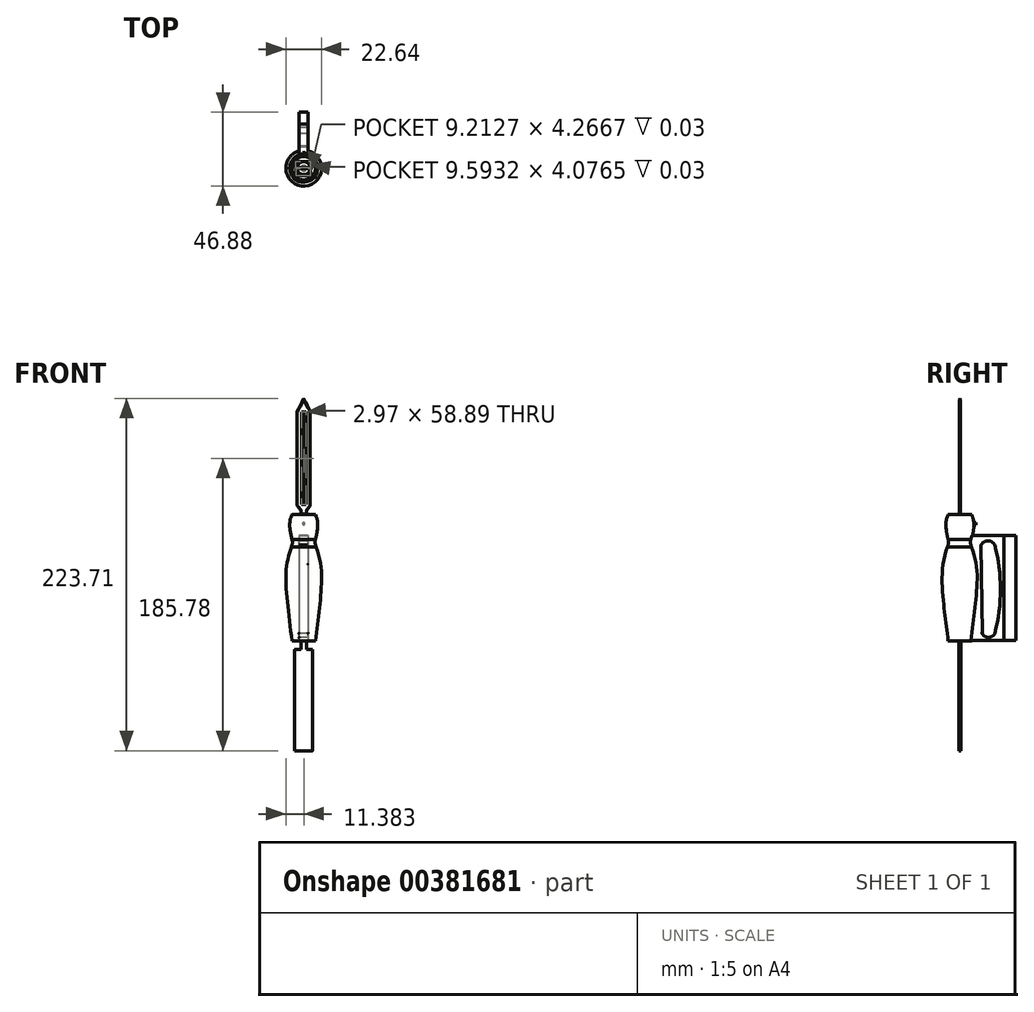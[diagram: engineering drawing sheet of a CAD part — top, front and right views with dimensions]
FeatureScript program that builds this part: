
annotation { "Feature Type Name" : "Feature", "Feature Type Description" : "" }
export const myFeature = defineFeature(function(context is Context, id is Id, definition is map)
    precondition{}
    {
        {
            var Q0;
            Q0=qCreatedBy(makeId("Front.planeOp"),FACE);
            var sketch = newSketch(context, id + "F0", { "sketchPlane" : qUnion([Q0])});
            skLineSegment(sketch, "E0", {"start": v(0, 19.44) * mm, "end": v(-7.47, 19.44) * mm});
            skLineSegment(sketch, "E1", {"start": v(-7.47, -61) * mm, "end": v(0, -61) * mm});
            skLineSegment(sketch, "E2", {"start": v(0, -61) * mm, "end": v(0, 19.44) * mm});
            skPoint(sketch, "E3.2.internal.orphan", {"position": v(-7.47, 3.27) * mm});
            skPoint(sketch, "E3.6.internal.orphan", {"position": v(-7.47, -61) * mm});
            skPoint(sketch, "E4.3.internal.orphan", {"position": v(-7.47, 0) * mm});
            skFitSpline(sketch, "E5", {"points": [v(-7.47, 19.44) * mm, v(-10.1, 11.25) * mm, v(-7.47, 3.27) * mm, v(-7.47, 0) * mm, v(-10.82, -8.71) * mm, v(-14.15, -22.97) * mm, v(-7.47, -61) * mm], "startDerivative": vector(-30.18, -56.03) * mm, "endDerivative": vector(34.52, -142.2) * mm});
            skFitSpline(sketch, "E6", {"points": [v(-7.47, 0) * mm, v(-10.82, -13.11) * mm, v(-10.82, -31.68) * mm, v(-7.47, -61) * mm], "startDerivative": vector(-14.77, -46.17) * mm, "endDerivative": vector(9.76, -75.95) * mm});
            skFitSpline(sketch, "E7", {"points": [v(-7.47, 19.44) * mm, v(-8.89, 13.54) * mm, v(-7.47, 3.27) * mm], "startDerivative": vector(-4.54, -12.63) * mm, "endDerivative": vector(4.15, -19.4) * mm});
            skSolve(sketch);
        }
        {
            var Q0;
            Q0=makeQuery(id+"F0.imprint","IMPRINT",FACE,{"disambiguationData":[TD([[makeQuery(id+"F0.imprint","IMPRINT",EDGE,{"derivedFrom":sQuery(id+"F0.wireOp",EDGE,"E0")}),1.0]])]});
            var Q1;
            Q1=sQuery(id+"F0.wireOp",EDGE,"E2");
            revolve(context, id + "F1", {"entities" : qUnion([Q0]), "axis" : qUnion([Q1]), "revolveType" : RevolveType.FULL});
        }
        {
            var Q0;
            Q0=qCreatedBy(makeId("Front.planeOp"),FACE);
            var sketch = newSketch(context, id + "F2", { "sketchPlane" : qUnion([Q0])});
            skLineSegment(sketch, "E8", {"start": v(0, 19.46) * mm, "end": v(0, 92.9) * mm});
            skLineSegment(sketch, "E9", {"start": v(0, 92.9) * mm, "end": v(-4.15, 84.7) * mm});
            skLineSegment(sketch, "E10", {"start": v(-4.15, 84.7) * mm, "end": v(-4.15, 24.88) * mm});
            skLineSegment(sketch, "E11", {"start": v(-4.15, 24.88) * mm, "end": v(-1.84, 21.73) * mm});
            skLineSegment(sketch, "E12", {"start": v(-1.84, 21.73) * mm, "end": v(-1.84, 19.45) * mm});
            skLineSegment(sketch, "E13", {"start": v(-1.84, 19.45) * mm, "end": v(0, 19.46) * mm});
            skSolve(sketch);
        }
        {
            var Q0;
            Q0=makeQuery(id+"F2.imprint","IMPRINT",FACE,{"disambiguationData":[TD([[makeQuery(id+"F2.imprint","IMPRINT",EDGE,{"derivedFrom":sQuery(id+"F2.wireOp",EDGE,"E8")}),1.0]])]});
            var Q1;
            Q1=sQuery(id+"F2.wireOp",EDGE,"E8");
            revolve(context, id + "F3", {"entities" : qUnion([Q0]), "axis" : qUnion([Q1]), "revolveType" : RevolveType.FULL});
        }
        {
            var Q0;
            Q0=qCreatedBy(makeId("Top.planeOp"),FACE);
            cPlane(context, id + "F4", {"entities" : qUnion([Q0]), "cplaneType" : CPlaneType.OFFSET, "offset" : 93.73 * mm, "width" : 152.4 * mm, "height" : 152.4 * mm});
        }
        {
            var Q0;
            Q0=qCreatedBy(id+"F4.planeOp",FACE);
            var sketch = newSketch(context, id + "F5", { "sketchPlane" : qUnion([Q0])});
            skLineSegment(sketch, "E14.bottom", {"start": v(4.35, -0.27) * mm, "end": v(-4.87, -0.27) * mm});
            skLineSegment(sketch, "E14.top", {"start": v(4.35, -4.54) * mm, "end": v(-4.87, -4.54) * mm});
            skLineSegment(sketch, "E14.left", {"start": v(4.35, -0.27) * mm, "end": v(4.35, -4.54) * mm});
            skLineSegment(sketch, "E14.right", {"start": v(-4.87, -0.27) * mm, "end": v(-4.87, -4.54) * mm});
            skLineSegment(sketch, "E15.bottom", {"start": v(4.37, 0.27) * mm, "end": v(-5.22, 0.27) * mm});
            skLineSegment(sketch, "E15.top", {"start": v(4.37, 4.35) * mm, "end": v(-5.22, 4.35) * mm});
            skLineSegment(sketch, "E15.left", {"start": v(4.37, 0.27) * mm, "end": v(4.37, 4.35) * mm});
            skLineSegment(sketch, "E15.right", {"start": v(-5.22, 0.27) * mm, "end": v(-5.22, 4.35) * mm});
            skSolve(sketch);
        }
        {
            var Q0;
            Q0=makeQuery(id+"F5.imprint","IMPRINT",FACE,{"disambiguationData":[TD([[makeQuery(id+"F5.imprint","IMPRINT",EDGE,{"derivedFrom":sQuery(id+"F5.wireOp",EDGE,"E15.bottom")}),-1.0]])]});
            var Q1;
            Q1=makeQuery(id+"F5.imprint","IMPRINT",FACE,{"disambiguationData":[TD([[makeQuery(id+"F5.imprint","IMPRINT",EDGE,{"derivedFrom":sQuery(id+"F5.wireOp",EDGE,"E14.bottom")}),1.0]])]});
            extrude(context, id + "F6", {"entities" : qUnion([Q0, Q1]), "operationType" : NewBodyOperationType.REMOVE, "oppositeDirection" : true, "depth" : 74.32 * mm});
        }
        {
            var Q0;
            Q0=qCreatedBy(makeId("Front.planeOp"),FACE);
            cPlane(context, id + "F7", {"entities" : qUnion([Q0]), "cplaneType" : CPlaneType.OFFSET, "offset" : 18.29 * mm, "width" : 152.4 * mm, "height" : 152.4 * mm});
        }
        {
            var Q0;
            Q0=qCreatedBy(id+"F7.planeOp",FACE);
            var sketch = newSketch(context, id + "F8", { "sketchPlane" : qUnion([Q0])});
            skLineSegment(sketch, "E16.bottom", {"start": v(-1.17, 84.42) * mm, "end": v(1.3, 84.42) * mm});
            skLineSegment(sketch, "E16.top", {"start": v(-1.17, 25.54) * mm, "end": v(1.3, 25.54) * mm});
            skLineSegment(sketch, "E16.left", {"start": v(-1.17, 84.42) * mm, "end": v(-1.17, 25.54) * mm});
            skLineSegment(sketch, "E16.right", {"start": v(1.3, 84.42) * mm, "end": v(1.3, 25.54) * mm});
            skSolve(sketch);
        }
        {
            var Q0;
            Q0=makeQuery(id+"F8.imprint","IMPRINT",FACE,{"disambiguationData":[TD([[makeQuery(id+"F8.imprint","IMPRINT",EDGE,{"derivedFrom":sQuery(id+"F8.wireOp",EDGE,"E16.bottom")}),-1.0]])]});
            extrude(context, id + "F9", {"entities" : qUnion([Q0]), "operationType" : NewBodyOperationType.REMOVE, "oppositeDirection" : true, "depth" : 25.4 * mm});
        }
        {
            var Q0;
            Q0=makeQuery(id+"F6.boolean.opBoolean","INTERSECT",EDGE,{"derivedFrom":[makeQuery(id+"F3.opRevolve","SWEPT_FACE",FACE,{"disambiguationData":[OSD([sQuery(id+"F2.wireOp",EDGE,"E9")])]}),makeQuery(id+"F6.opExtrude","SWEPT_FACE",FACE,{"disambiguationData":[OSD([sQuery(id+"F5.wireOp",EDGE,"E14.bottom")])]})]});
            var Q1;
            Q1=makeQuery(id+"F6.boolean.opBoolean","INTERSECT",EDGE,{"disambiguationData":[OD(1.0)],"derivedFrom":[makeQuery(id+"F3.opRevolve","SWEPT_FACE",FACE,{"disambiguationData":[OSD([sQuery(id+"F2.wireOp",EDGE,"E10")])]}),makeQuery(id+"F6.opExtrude","SWEPT_FACE",FACE,{"disambiguationData":[OSD([sQuery(id+"F5.wireOp",EDGE,"E14.bottom")])]})]});
            var Q2;
            Q2=makeQuery(id+"F6.boolean.opBoolean","INTERSECT",EDGE,{"disambiguationData":[OD(0.0)],"derivedFrom":[makeQuery(id+"F3.opRevolve","SWEPT_FACE",FACE,{"disambiguationData":[OSD([sQuery(id+"F2.wireOp",EDGE,"E10")])]}),makeQuery(id+"F6.opExtrude","SWEPT_FACE",FACE,{"disambiguationData":[OSD([sQuery(id+"F5.wireOp",EDGE,"E14.bottom")])]})]});
            var Q3;
            Q3=makeQuery(id+"F6.boolean.opBoolean","INTERSECT",EDGE,{"disambiguationData":[OD(0.0)],"derivedFrom":[makeQuery(id+"F3.opRevolve","SWEPT_FACE",FACE,{"disambiguationData":[OSD([sQuery(id+"F2.wireOp",EDGE,"E11")])]}),makeQuery(id+"F6.opExtrude","SWEPT_FACE",FACE,{"disambiguationData":[OSD([sQuery(id+"F5.wireOp",EDGE,"E14.bottom")])]})]});
            var Q4;
            Q4=makeQuery(id+"F6.boolean.opBoolean","INTERSECT",EDGE,{"disambiguationData":[OD(1.0)],"derivedFrom":[makeQuery(id+"F3.opRevolve","SWEPT_FACE",FACE,{"disambiguationData":[OSD([sQuery(id+"F2.wireOp",EDGE,"E11")])]}),makeQuery(id+"F6.opExtrude","SWEPT_FACE",FACE,{"disambiguationData":[OSD([sQuery(id+"F5.wireOp",EDGE,"E14.bottom")])]})]});
            var Q5;
            Q5=makeQuery(id+"F6.boolean.opBoolean","INTERSECT",EDGE,{"derivedFrom":[makeQuery(id+"F3.opRevolve","SWEPT_FACE",FACE,{"disambiguationData":[OSD([sQuery(id+"F2.wireOp",EDGE,"E9")])]}),makeQuery(id+"F6.opExtrude","SWEPT_FACE",FACE,{"disambiguationData":[OSD([sQuery(id+"F5.wireOp",EDGE,"E15.bottom")])]})]});
            var Q6;
            Q6=makeQuery(id+"F6.boolean.opBoolean","INTERSECT",EDGE,{"disambiguationData":[OD(0.0)],"derivedFrom":[makeQuery(id+"F3.opRevolve","SWEPT_FACE",FACE,{"disambiguationData":[OSD([sQuery(id+"F2.wireOp",EDGE,"E10")])]}),makeQuery(id+"F6.opExtrude","SWEPT_FACE",FACE,{"disambiguationData":[OSD([sQuery(id+"F5.wireOp",EDGE,"E15.bottom")])]})]});
            var Q7;
            Q7=makeQuery(id+"F6.boolean.opBoolean","SPLIT",FACE,{"disambiguationData":[OD(1.0)],"derivedFrom":makeQuery(id+"F3.opRevolve","SWEPT_FACE",FACE,{"disambiguationData":[OSD([sQuery(id+"F2.wireOp",EDGE,"E10")])]})});
            var Q8;
            Q8=makeQuery(id+"F6.boolean.opBoolean","INTERSECT",EDGE,{"disambiguationData":[OD(1.0)],"derivedFrom":[makeQuery(id+"F3.opRevolve","SWEPT_FACE",FACE,{"disambiguationData":[OSD([sQuery(id+"F2.wireOp",EDGE,"E11")])]}),makeQuery(id+"F6.opExtrude","SWEPT_FACE",FACE,{"disambiguationData":[OSD([sQuery(id+"F5.wireOp",EDGE,"E15.bottom")])]})]});
            var Q9;
            Q9=makeQuery(id+"F6.boolean.opBoolean","INTERSECT",EDGE,{"disambiguationData":[OD(0.0)],"derivedFrom":[makeQuery(id+"F3.opRevolve","SWEPT_FACE",FACE,{"disambiguationData":[OSD([sQuery(id+"F2.wireOp",EDGE,"E11")])]}),makeQuery(id+"F6.opExtrude","SWEPT_FACE",FACE,{"disambiguationData":[OSD([sQuery(id+"F5.wireOp",EDGE,"E15.bottom")])]})]});
            fillet(context, id + "F10", {"entities" : qUnion([Q0, Q1, Q2, Q3, Q4, Q5, Q6, Q7, Q8, Q9]), "radius" : 0.25 * mm, "tangentPropagation" : true, "allowEdgeOverflow" : false});
        }
        {
            var Q0;
            Q0=makeQuery(id+"F9.boolean.opBoolean","INTERSECT",EDGE,{"derivedFrom":[makeQuery(id+"F6.boolean.opBoolean","COPY",FACE,{"derivedFrom":makeQuery(id+"F6.opExtrude","SWEPT_FACE",FACE,{"disambiguationData":[OSD([sQuery(id+"F5.wireOp",EDGE,"E15.bottom")])]})}),makeQuery(id+"F9.opExtrude","SWEPT_FACE",FACE,{"disambiguationData":[OSD([sQuery(id+"F8.wireOp",EDGE,"E16.right")])]})]});
            var Q1;
            Q1=makeQuery(id+"F9.boolean.opBoolean","INTERSECT",EDGE,{"derivedFrom":[makeQuery(id+"F6.boolean.opBoolean","COPY",FACE,{"derivedFrom":makeQuery(id+"F6.opExtrude","SWEPT_FACE",FACE,{"disambiguationData":[OSD([sQuery(id+"F5.wireOp",EDGE,"E15.bottom")])]})}),makeQuery(id+"F9.opExtrude","SWEPT_FACE",FACE,{"disambiguationData":[OSD([sQuery(id+"F8.wireOp",EDGE,"E16.left")])]})]});
            var Q2;
            Q2=makeQuery(id+"F9.boolean.opBoolean","INTERSECT",EDGE,{"derivedFrom":[makeQuery(id+"F6.boolean.opBoolean","COPY",FACE,{"derivedFrom":makeQuery(id+"F6.opExtrude","SWEPT_FACE",FACE,{"disambiguationData":[OSD([sQuery(id+"F5.wireOp",EDGE,"E14.bottom")])]})}),makeQuery(id+"F9.opExtrude","SWEPT_FACE",FACE,{"disambiguationData":[OSD([sQuery(id+"F8.wireOp",EDGE,"E16.left")])]})]});
            var Q3;
            Q3=makeQuery(id+"F9.boolean.opBoolean","INTERSECT",EDGE,{"derivedFrom":[makeQuery(id+"F6.boolean.opBoolean","COPY",FACE,{"derivedFrom":makeQuery(id+"F6.opExtrude","SWEPT_FACE",FACE,{"disambiguationData":[OSD([sQuery(id+"F5.wireOp",EDGE,"E14.bottom")])]})}),makeQuery(id+"F9.opExtrude","SWEPT_FACE",FACE,{"disambiguationData":[OSD([sQuery(id+"F8.wireOp",EDGE,"E16.right")])]})]});
            chamfer(context, id + "F11", {"entities" : qUnion([Q0, Q1, Q2, Q3]), "width" : 0.25 * mm, "tangentPropagation" : true});
        }
        {
            var Q0;
            Q0=qCreatedBy(makeId("Front.planeOp"),FACE);
            cPlane(context, id + "F12", {"entities" : qUnion([Q0]), "cplaneType" : CPlaneType.OFFSET, "offset" : 8.79 * mm, "oppositeDirection" : true, "width" : 152.4 * mm, "height" : 152.4 * mm});
        }
        {
            var Q0;
            Q0=qCreatedBy(id+"F12.planeOp",FACE);
            var sketch = newSketch(context, id + "F13", { "sketchPlane" : qUnion([Q0])});
            skCircle(sketch, "E17", {"center": v(0, 13.43) * mm, "radius": 0.68 * mm});
            skSolve(sketch);
        }
        {
            var Q0;
            Q0=makeQuery(id+"F13.imprint","IMPRINT",FACE,{"disambiguationData":[TD([[makeQuery(id+"F13.imprint","IMPRINT",EDGE,{"derivedFrom":sQuery(id+"F13.wireOp",EDGE,"E17")}),1.0]])]});
            extrude(context, id + "F14", {"entities" : qUnion([Q0]), "operationType" : NewBodyOperationType.ADD, "oppositeDirection" : true, "depth" : 1.24 * mm});
        }
        {
            var Q0;
            Q0=qCreatedBy(makeId("Front.planeOp"),FACE);
            cPlane(context, id + "F15", {"entities" : qUnion([Q0]), "cplaneType" : CPlaneType.OFFSET, "offset" : 6.6 * mm, "oppositeDirection" : true, "width" : 152.4 * mm, "height" : 152.4 * mm});
        }
        {
            var Q0;
            Q0=qCreatedBy(id+"F15.planeOp",FACE);
            var sketch = newSketch(context, id + "F16", { "sketchPlane" : qUnion([Q0])});
            skLineSegment(sketch, "E18.bottom", {"start": v(-3.1, 5.9) * mm, "end": v(2.7, 5.9) * mm});
            skLineSegment(sketch, "E18.top", {"start": v(-3.1, -60.67) * mm, "end": v(2.7, -60.67) * mm});
            skLineSegment(sketch, "E18.left", {"start": v(-3.1, 5.9) * mm, "end": v(-3.1, -60.67) * mm});
            skLineSegment(sketch, "E18.right", {"start": v(2.7, 5.9) * mm, "end": v(2.7, -60.67) * mm});
            skSolve(sketch);
        }
        {
            var Q0;
            Q0=makeQuery(id+"F16.imprint","IMPRINT",FACE,{"disambiguationData":[TD([[makeQuery(id+"F16.imprint","IMPRINT",EDGE,{"derivedFrom":sQuery(id+"F16.wireOp",EDGE,"E18.bottom")}),-1.0]])]});
            extrude(context, id + "F17", {"entities" : qUnion([Q0]), "operationType" : NewBodyOperationType.ADD, "oppositeDirection" : true, "depth" : 21.34 * mm});
        }
        {
            var Q0;
            Q0=qCreatedBy(makeId("Right.planeOp"),FACE);
            cPlane(context, id + "F18", {"entities" : qUnion([Q0]), "cplaneType" : CPlaneType.OFFSET, "offset" : 7.87 * mm, "oppositeDirection" : true, "width" : 152.4 * mm, "height" : 152.4 * mm});
        }
        {
            var Q0;
            Q0=qCreatedBy(id+"F18.planeOp",FACE);
            var sketch = newSketch(context, id + "F19", { "sketchPlane" : qUnion([Q0])});
            skArc(sketch, "E19", {"start": v(22.14, 0) * mm, "mid": v(17.8, 2.52) * mm, "end": v(13.44, 0) * mm});
            skArc(sketch, "E20", {"start": v(22.14, -56.25) * mm, "mid": v(25.8, -28.12) * mm, "end": v(22.14, 0) * mm});
            skArc(sketch, "E21", {"start": v(14.15, -56.25) * mm, "mid": v(18.15, -58.76) * mm, "end": v(22.14, -56.25) * mm});
            skLineSegment(sketch, "E22", {"start": v(13.44, 0) * mm, "end": v(14.15, -56.25) * mm});
            skSolve(sketch);
        }
        {
            var Q0;
            Q0=makeQuery(id+"F19.imprint","IMPRINT",FACE,{"disambiguationData":[TD([[makeQuery(id+"F19.imprint","IMPRINT",EDGE,{"derivedFrom":sQuery(id+"F19.wireOp",EDGE,"E19")}),1.0]])]});
            extrude(context, id + "F20", {"entities" : qUnion([Q0]), "operationType" : NewBodyOperationType.REMOVE, "depth" : 25.4 * mm});
        }
        {
            var Q0;
            Q0=makeQuery(id+"F20.boolean.opBoolean","INTERSECT",EDGE,{"derivedFrom":[makeQuery(id+"F17.opExtrude","SWEPT_FACE",FACE,{"disambiguationData":[OSD([sQuery(id+"F16.wireOp",EDGE,"E18.left")])]}),makeQuery(id+"F20.opExtrude","SWEPT_FACE",FACE,{"disambiguationData":[OSD([sQuery(id+"F19.wireOp",EDGE,"E22")])]})]});
            var Q1;
            Q1=makeQuery(id+"F20.boolean.opBoolean","INTERSECT",EDGE,{"derivedFrom":[makeQuery(id+"F17.opExtrude","SWEPT_FACE",FACE,{"disambiguationData":[OSD([sQuery(id+"F16.wireOp",EDGE,"E18.left")])]}),makeQuery(id+"F20.opExtrude","SWEPT_FACE",FACE,{"disambiguationData":[OSD([sQuery(id+"F19.wireOp",EDGE,"E21")])]})]});
            var Q2;
            Q2=makeQuery(id+"F20.boolean.opBoolean","INTERSECT",EDGE,{"derivedFrom":[makeQuery(id+"F17.opExtrude","SWEPT_FACE",FACE,{"disambiguationData":[OSD([sQuery(id+"F16.wireOp",EDGE,"E18.right")])]}),makeQuery(id+"F20.opExtrude","SWEPT_FACE",FACE,{"disambiguationData":[OSD([sQuery(id+"F19.wireOp",EDGE,"E22")])]})]});
            fillet(context, id + "F21", {"entities" : qUnion([Q0, Q1, Q2]), "radius" : 0.25 * mm, "tangentPropagation" : true, "allowEdgeOverflow" : false});
        }
        {
            var Q0;
            Q0=qCreatedBy(makeId("Front.planeOp"),FACE);
            var sketch = newSketch(context, id + "F22", { "sketchPlane" : qUnion([Q0])});
            skLineSegment(sketch, "E23", {"start": v(0, -61) * mm, "end": v(0, -130.8) * mm});
            skLineSegment(sketch, "E24", {"start": v(0, -130.8) * mm, "end": v(-5.7, -130.8) * mm});
            skLineSegment(sketch, "E25", {"start": v(-5.7, -130.8) * mm, "end": v(-5.7, -66.47) * mm});
            skLineSegment(sketch, "E26", {"start": v(-5.7, -66.47) * mm, "end": v(-1.75, -66.47) * mm});
            skLineSegment(sketch, "E27", {"start": v(-1.75, -66.47) * mm, "end": v(-1.75, -61) * mm});
            skLineSegment(sketch, "E28", {"start": v(-1.75, -61) * mm, "end": v(0, -61) * mm});
            skSolve(sketch);
        }
        {
            var Q0;
            Q0=makeQuery(id+"F22.imprint","IMPRINT",FACE,{"disambiguationData":[TD([[makeQuery(id+"F22.imprint","IMPRINT",EDGE,{"derivedFrom":sQuery(id+"F22.wireOp",EDGE,"E23")}),-1.0]])]});
            var Q1;
            Q1=sQuery(id+"F22.wireOp",EDGE,"E23");
            revolve(context, id + "F23", {"entities" : qUnion([Q0]), "axis" : qUnion([Q1]), "revolveType" : RevolveType.FULL});
        }
        {
            var Q0;
            Q0=qCreatedBy(makeId("Top.planeOp"),FACE);
            cPlane(context, id + "F24", {"entities" : qUnion([Q0]), "cplaneType" : CPlaneType.OFFSET, "offset" : 133.86 * mm, "oppositeDirection" : true, "width" : 152.4 * mm, "height" : 152.4 * mm});
        }
        {
            var Q0;
            Q0=qCreatedBy(id+"F24.planeOp",FACE);
            var sketch = newSketch(context, id + "F25", { "sketchPlane" : qUnion([Q0])});
            skLineSegment(sketch, "E29.bottom", {"start": v(5.83, -0.51) * mm, "end": v(-6.39, -0.51) * mm});
            skLineSegment(sketch, "E29.top", {"start": v(5.83, -6.23) * mm, "end": v(-6.39, -6.23) * mm});
            skLineSegment(sketch, "E29.left", {"start": v(5.83, -0.51) * mm, "end": v(5.83, -6.23) * mm});
            skLineSegment(sketch, "E29.right", {"start": v(-6.39, -0.51) * mm, "end": v(-6.39, -6.23) * mm});
            skLineSegment(sketch, "E30.bottom", {"start": v(-6.39, 0.52) * mm, "end": v(5.91, 0.52) * mm});
            skLineSegment(sketch, "E30.top", {"start": v(-6.39, 5.87) * mm, "end": v(5.91, 5.87) * mm});
            skLineSegment(sketch, "E30.left", {"start": v(-6.39, 0.52) * mm, "end": v(-6.39, 5.87) * mm});
            skLineSegment(sketch, "E30.right", {"start": v(5.91, 0.52) * mm, "end": v(5.91, 5.87) * mm});
            skSolve(sketch);
        }
        {
            var Q0;
            Q0=makeQuery(id+"F25.imprint","IMPRINT",FACE,{"disambiguationData":[TD([[makeQuery(id+"F25.imprint","IMPRINT",EDGE,{"derivedFrom":sQuery(id+"F25.wireOp",EDGE,"E29.bottom")}),1.0]])]});
            var Q1;
            Q1=makeQuery(id+"F25.imprint","IMPRINT",FACE,{"disambiguationData":[TD([[makeQuery(id+"F25.imprint","IMPRINT",EDGE,{"derivedFrom":sQuery(id+"F25.wireOp",EDGE,"E30.bottom")}),1.0]])]});
            extrude(context, id + "F26", {"entities" : qUnion([Q0, Q1]), "operationType" : NewBodyOperationType.REMOVE, "depth" : 72.8 * mm});
        }
        {
            var Q0;
            Q0=qCreatedBy(id+"F12.planeOp",FACE);
            cPlane(context, id + "F27", {"entities" : qUnion([Q0]), "cplaneType" : CPlaneType.OFFSET, "offset" : 19.15 * mm, "oppositeDirection" : true, "width" : 152.4 * mm, "height" : 152.4 * mm});
        }
        {
            var Q0;
            Q0=qCreatedBy(id+"F27.planeOp",FACE);
            var sketch = newSketch(context, id + "F28", { "sketchPlane" : qUnion([Q0])});
            skLineSegment(sketch, "E31.bottom", {"start": v(2.7, 5.9) * mm, "end": v(-3.1, 5.9) * mm});
            skLineSegment(sketch, "E31.top", {"start": v(2.7, -60.67) * mm, "end": v(-3.1, -60.67) * mm});
            skLineSegment(sketch, "E31.left", {"start": v(2.7, 5.9) * mm, "end": v(2.7, -60.67) * mm});
            skLineSegment(sketch, "E31.right", {"start": v(-3.1, 5.9) * mm, "end": v(-3.1, -60.67) * mm});
            skSolve(sketch);
        }
        {
            var Q0;
            Q0=makeQuery(id+"F28.imprint","IMPRINT",FACE,{"disambiguationData":[TD([[makeQuery(id+"F28.imprint","IMPRINT",EDGE,{"derivedFrom":sQuery(id+"F28.wireOp",EDGE,"E31.bottom")}),1.0]])]});
            extrude(context, id + "F29", {"entities" : qUnion([Q0]), "oppositeDirection" : true, "depth" : 7.62 * mm});
        }
    });
